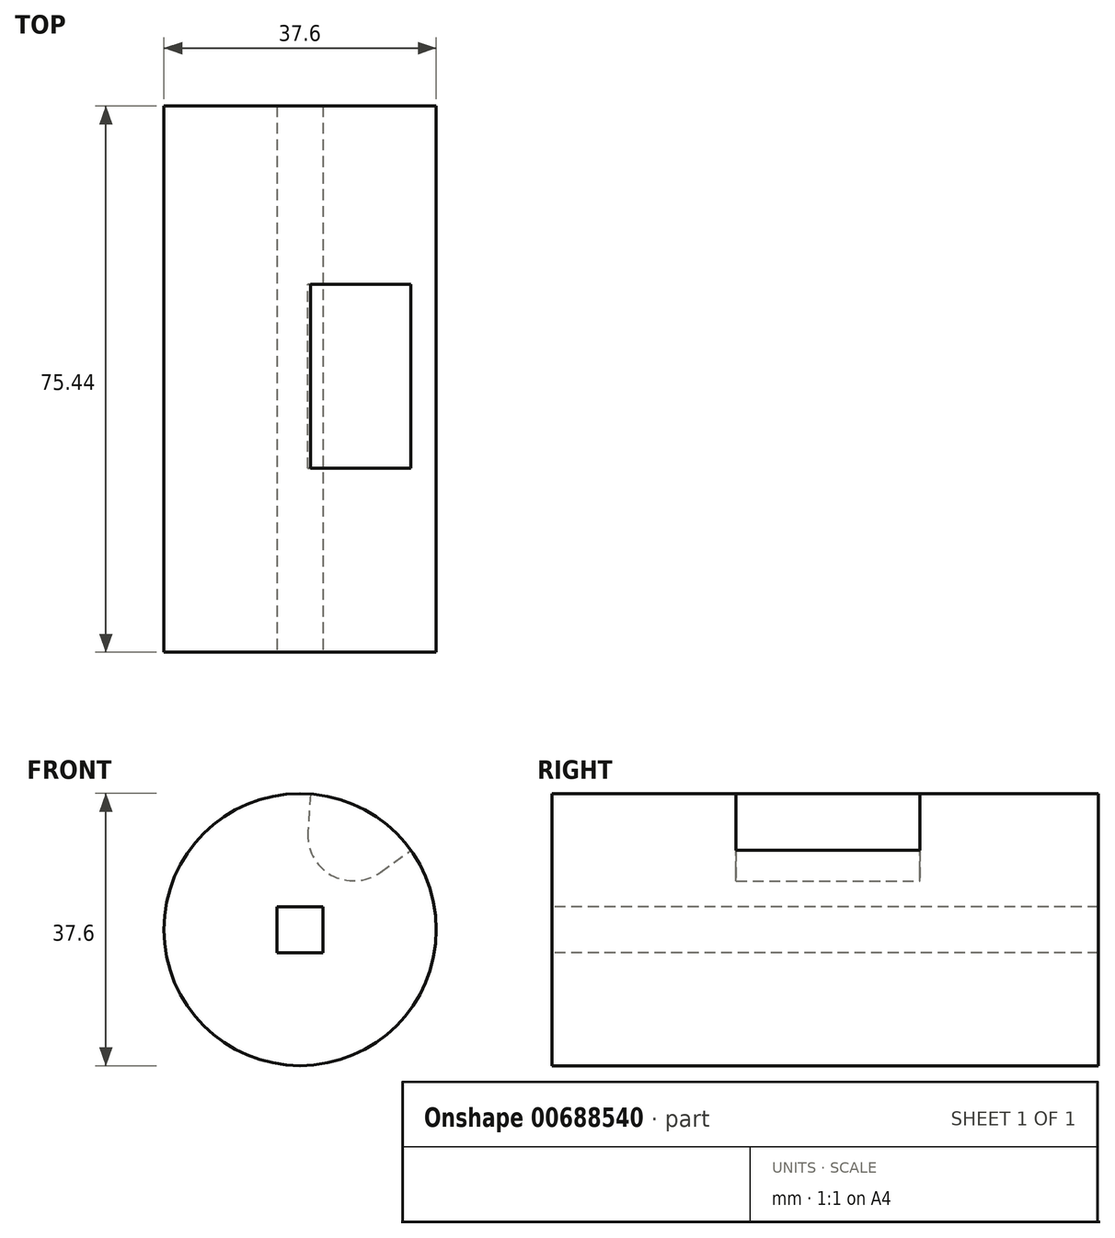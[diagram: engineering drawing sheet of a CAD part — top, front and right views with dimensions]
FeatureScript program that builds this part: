
annotation { "Feature Type Name" : "Feature", "Feature Type Description" : "" }
export const myFeature = defineFeature(function(context is Context, id is Id, definition is map)
    precondition{}
    {
        {
            var Q0;
            Q0=qCreatedBy(makeId("Front.planeOp"),FACE);
            var sketch = newSketch(context, id + "F0", { "sketchPlane" : qUnion([Q0])});
            skCircle(sketch, "E0", {"center": v(0, 0) * mm, "radius": 18.8 * mm});
            skSolve(sketch);
        }
        {
            var Q0;
            Q0=qSketchRegion(id+"F0",true);
            extrude(context, id + "F1", {"entities" : qUnion([Q0]), "depth" : 75.44 * mm, "offsetDistance" : 25.4 * mm});
        }
        {
            var Q0;
            Q0=makeQuery(id+"F1.opExtrude","CAP_FACE",FACE,{"disambiguationData":[OSD([sQuery(id+"F0.wireOp",EDGE,"E0")])],"isStart":false});
            cPlane(context, id + "F2", {"entities" : qUnion([Q0]), "cplaneType" : CPlaneType.OFFSET, "offset" : 38.1 * mm, "oppositeDirection" : true, "width" : 152.4 * mm, "height" : 152.4 * mm});
        }
        {
            var Q0;
            Q0=qCreatedBy(id+"F2.planeOp",FACE);
            var sketch = newSketch(context, id + "F3", { "sketchPlane" : qUnion([Q0])});
            skArc(sketch, "E1.0", {"start": v(9.1, 16.45) * mm, "mid": v(6.54, 17.62) * mm, "end": v(3.84, 18.4) * mm});
            skArc(sketch, "E2.0", {"start": v(15.3, 10.93) * mm, "mid": v(9.24, 16.37) * mm, "end": v(1.46, 18.74) * mm});
            skLineSegment(sketch, "E3", {"start": v(1.46, 18.74) * mm, "end": v(1.06, 13.58) * mm});
            skLineSegment(sketch, "E4", {"start": v(11.08, 7.92) * mm, "end": v(15.3, 10.93) * mm});
            skArc(sketch, "E5.filletArc", {"start": v(1.06, 13.58) * mm, "mid": v(4.27, 7.55) * mm, "end": v(11.08, 7.92) * mm});
            skSolve(sketch);
        }
        {
            var Q0;
            Q0=qSketchRegion(id+"F3",true);
            extrude(context, id + "F4", {"entities" : qUnion([Q0]), "operationType" : NewBodyOperationType.REMOVE, "endBound" : BoundingType.SYMMETRIC, "depth" : 25.4 * mm, "offsetDistance" : 25.4 * mm});
        }
        {
            var Q0;
            Q0=makeQuery(id+"F1.opExtrude","CAP_FACE",FACE,{"disambiguationData":[OSD([sQuery(id+"F0.wireOp",EDGE,"E0")])],"isStart":false});
            var sketch = newSketch(context, id + "F5", { "sketchPlane" : qUnion([Q0])});
            skLineSegment(sketch, "E6.bottom", {"start": v(3.18, -3.17) * mm, "end": v(-3.17, -3.18) * mm});
            skLineSegment(sketch, "E6.top", {"start": v(3.17, 3.18) * mm, "end": v(-3.18, 3.18) * mm});
            skLineSegment(sketch, "E6.left", {"start": v(3.18, -3.17) * mm, "end": v(3.17, 3.18) * mm});
            skLineSegment(sketch, "E6.right", {"start": v(-3.17, -3.18) * mm, "end": v(-3.18, 3.18) * mm});
            skPoint(sketch, "E6.middle", {"position": v(0, 0) * mm});
            skSolve(sketch);
        }
        {
            var Q0;
            Q0=qSketchRegion(id+"F5",true);
            extrude(context, id + "F6", {"entities" : qUnion([Q0]), "operationType" : NewBodyOperationType.REMOVE, "oppositeDirection" : true, "depth" : 105.66 * mm, "offsetDistance" : 25.4 * mm});
        }
    });
